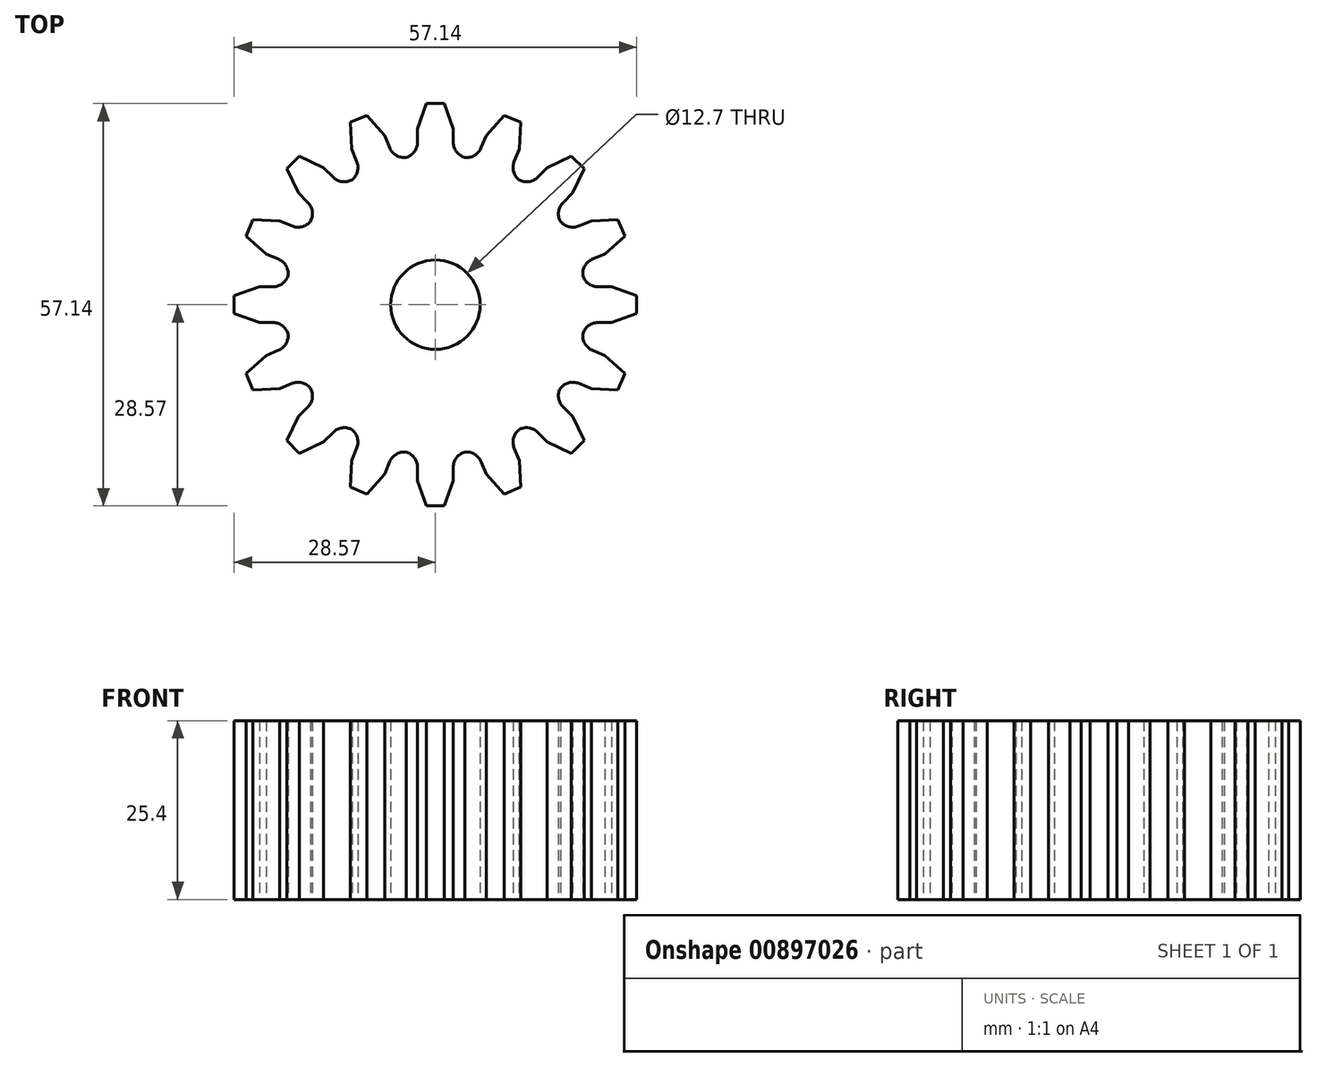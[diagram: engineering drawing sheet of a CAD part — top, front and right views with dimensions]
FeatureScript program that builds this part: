
annotation { "Feature Type Name" : "Feature", "Feature Type Description" : "" }
export const myFeature = defineFeature(function(context is Context, id is Id, definition is map)
    precondition{}
    {
        {
            var Q0;
            Q0=qCreatedBy(makeId("Top.planeOp"),FACE);
            var sketch = newSketch(context, id + "F0", { "sketchPlane" : qUnion([Q0])});
            skCircle(sketch, "E0", {"center": v(0, 0) * mm, "radius": 6.35 * mm});
            skLineSegment(sketch, "E1", {"start": v(0, 28.58) * mm, "end": v(1.27, 28.58) * mm});
            skLineSegment(sketch, "E2", {"start": v(0, 28.58) * mm, "end": v(-1.27, 28.58) * mm});
            skLineSegment(sketch, "E3", {"start": v(-1.27, 28.58) * mm, "end": v(-2.54, 24.98) * mm});
            skLineSegment(sketch, "E4", {"start": v(2.54, 24.98) * mm, "end": v(1.27, 28.58) * mm});
            skPoint(sketch, "E5.MirrorCS.start.orphan", {"position": v(-2.54, 28.58) * mm});
            skPoint(sketch, "E6.orphan", {"position": v(2.54, 28.58) * mm});
            skLineSegment(sketch, "E7.1.2", {"start": v(-12.1, 25.91) * mm, "end": v(-11.9, 22.1) * mm});
            skLineSegment(sketch, "E7.1.4", {"start": v(-7.21, 24.05) * mm, "end": v(-9.76, 26.89) * mm});
            skLineSegment(sketch, "E7.1.5", {"start": v(-10.94, 26.4) * mm, "end": v(-12.1, 25.91) * mm});
            skLineSegment(sketch, "E7.1.6", {"start": v(-10.94, 26.4) * mm, "end": v(-9.76, 26.89) * mm});
            skLineSegment(sketch, "E7.2.2", {"start": v(-21.1, 19.3) * mm, "end": v(-19.46, 15.87) * mm});
            skLineSegment(sketch, "E7.2.4", {"start": v(-15.87, 19.46) * mm, "end": v(-19.3, 21.1) * mm});
            skLineSegment(sketch, "E7.2.5", {"start": v(-20.2, 20.2) * mm, "end": v(-21.1, 19.3) * mm});
            skLineSegment(sketch, "E7.2.6", {"start": v(-20.2, 20.2) * mm, "end": v(-19.3, 21.1) * mm});
            skLineSegment(sketch, "E7.3.2", {"start": v(-26.89, 9.76) * mm, "end": v(-24.05, 7.21) * mm});
            skLineSegment(sketch, "E7.3.4", {"start": v(-22.1, 11.9) * mm, "end": v(-25.91, 12.1) * mm});
            skLineSegment(sketch, "E7.3.5", {"start": v(-26.4, 10.94) * mm, "end": v(-26.89, 9.76) * mm});
            skLineSegment(sketch, "E7.3.6", {"start": v(-26.4, 10.94) * mm, "end": v(-25.91, 12.1) * mm});
            skLineSegment(sketch, "E7.4.2", {"start": v(-28.58, -1.27) * mm, "end": v(-24.98, -2.54) * mm});
            skLineSegment(sketch, "E7.4.4", {"start": v(-24.98, 2.54) * mm, "end": v(-28.58, 1.27) * mm});
            skLineSegment(sketch, "E7.4.5", {"start": v(-28.58, 0) * mm, "end": v(-28.58, -1.27) * mm});
            skLineSegment(sketch, "E7.4.6", {"start": v(-28.58, 0) * mm, "end": v(-28.58, 1.27) * mm});
            skLineSegment(sketch, "E7.5.1", {"start": v(-22.1, -11.9) * mm, "end": v(-20.34, -11.18) * mm});
            skLineSegment(sketch, "E7.5.2", {"start": v(-25.91, -12.1) * mm, "end": v(-22.1, -11.9) * mm});
            skLineSegment(sketch, "E7.5.4", {"start": v(-24.05, -7.21) * mm, "end": v(-26.89, -9.76) * mm});
            skLineSegment(sketch, "E7.5.5", {"start": v(-26.4, -10.94) * mm, "end": v(-25.91, -12.1) * mm});
            skLineSegment(sketch, "E7.5.6", {"start": v(-26.4, -10.94) * mm, "end": v(-26.89, -9.76) * mm});
            skLineSegment(sketch, "E7.6.2", {"start": v(-19.3, -21.1) * mm, "end": v(-15.87, -19.46) * mm});
            skLineSegment(sketch, "E7.6.3", {"start": v(-19.46, -15.87) * mm, "end": v(-18.11, -14.52) * mm});
            skLineSegment(sketch, "E7.6.4", {"start": v(-19.46, -15.87) * mm, "end": v(-21.1, -19.3) * mm});
            skLineSegment(sketch, "E7.6.5", {"start": v(-20.2, -20.2) * mm, "end": v(-19.3, -21.1) * mm});
            skLineSegment(sketch, "E7.6.6", {"start": v(-20.2, -20.2) * mm, "end": v(-21.1, -19.3) * mm});
            skLineSegment(sketch, "E7.7.2", {"start": v(-9.76, -26.89) * mm, "end": v(-7.21, -24.05) * mm});
            skLineSegment(sketch, "E7.7.4", {"start": v(-11.9, -22.1) * mm, "end": v(-12.1, -25.91) * mm});
            skLineSegment(sketch, "E7.7.5", {"start": v(-10.94, -26.4) * mm, "end": v(-9.76, -26.89) * mm});
            skLineSegment(sketch, "E7.7.6", {"start": v(-10.94, -26.4) * mm, "end": v(-12.1, -25.91) * mm});
            skLineSegment(sketch, "E7.8.2", {"start": v(1.27, -28.58) * mm, "end": v(2.54, -24.98) * mm});
            skLineSegment(sketch, "E7.8.4", {"start": v(-2.54, -24.98) * mm, "end": v(-1.27, -28.58) * mm});
            skLineSegment(sketch, "E7.8.5", {"start": v(0, -28.58) * mm, "end": v(1.27, -28.58) * mm});
            skLineSegment(sketch, "E7.8.6", {"start": v(0, -28.58) * mm, "end": v(-1.27, -28.58) * mm});
            skLineSegment(sketch, "E7.9.2", {"start": v(12.1, -25.91) * mm, "end": v(11.9, -22.1) * mm});
            skLineSegment(sketch, "E7.9.4", {"start": v(7.21, -24.05) * mm, "end": v(9.76, -26.89) * mm});
            skLineSegment(sketch, "E7.9.5", {"start": v(10.94, -26.4) * mm, "end": v(12.1, -25.91) * mm});
            skLineSegment(sketch, "E7.9.6", {"start": v(10.94, -26.4) * mm, "end": v(9.76, -26.89) * mm});
            skLineSegment(sketch, "E7.10.2", {"start": v(21.1, -19.3) * mm, "end": v(19.46, -15.87) * mm});
            skLineSegment(sketch, "E7.10.3", {"start": v(15.87, -19.46) * mm, "end": v(13.18, -16.78) * mm});
            skLineSegment(sketch, "E7.10.4", {"start": v(15.87, -19.46) * mm, "end": v(19.3, -21.1) * mm});
            skLineSegment(sketch, "E7.10.5", {"start": v(20.2, -20.2) * mm, "end": v(21.1, -19.3) * mm});
            skLineSegment(sketch, "E7.10.6", {"start": v(20.2, -20.2) * mm, "end": v(19.3, -21.1) * mm});
            skLineSegment(sketch, "E7.11.2", {"start": v(26.89, -9.76) * mm, "end": v(24.05, -7.21) * mm});
            skLineSegment(sketch, "E7.11.4", {"start": v(22.1, -11.9) * mm, "end": v(25.91, -12.1) * mm});
            skLineSegment(sketch, "E7.11.5", {"start": v(26.4, -10.94) * mm, "end": v(26.89, -9.76) * mm});
            skLineSegment(sketch, "E7.11.6", {"start": v(26.4, -10.94) * mm, "end": v(25.91, -12.1) * mm});
            skLineSegment(sketch, "E7.12.2", {"start": v(28.58, 1.27) * mm, "end": v(24.98, 2.54) * mm});
            skLineSegment(sketch, "E7.12.4", {"start": v(24.98, -2.54) * mm, "end": v(28.58, -1.27) * mm});
            skLineSegment(sketch, "E7.12.5", {"start": v(28.58, 0) * mm, "end": v(28.58, 1.27) * mm});
            skLineSegment(sketch, "E7.12.6", {"start": v(28.58, 0) * mm, "end": v(28.58, -1.27) * mm});
            skLineSegment(sketch, "E7.13.2", {"start": v(25.91, 12.1) * mm, "end": v(22.1, 11.9) * mm});
            skLineSegment(sketch, "E7.13.4", {"start": v(24.05, 7.21) * mm, "end": v(26.89, 9.76) * mm});
            skLineSegment(sketch, "E7.13.5", {"start": v(26.4, 10.94) * mm, "end": v(25.91, 12.1) * mm});
            skLineSegment(sketch, "E7.13.6", {"start": v(26.4, 10.94) * mm, "end": v(26.89, 9.76) * mm});
            skLineSegment(sketch, "E7.14.2", {"start": v(19.3, 21.1) * mm, "end": v(15.87, 19.46) * mm});
            skLineSegment(sketch, "E7.14.4", {"start": v(19.46, 15.87) * mm, "end": v(21.1, 19.3) * mm});
            skLineSegment(sketch, "E7.14.5", {"start": v(20.2, 20.2) * mm, "end": v(19.3, 21.1) * mm});
            skLineSegment(sketch, "E7.14.6", {"start": v(20.2, 20.2) * mm, "end": v(21.1, 19.3) * mm});
            skLineSegment(sketch, "E7.15.2", {"start": v(9.76, 26.89) * mm, "end": v(7.21, 24.05) * mm});
            skLineSegment(sketch, "E7.15.4", {"start": v(11.9, 22.1) * mm, "end": v(12.1, 25.91) * mm});
            skLineSegment(sketch, "E7.15.5", {"start": v(10.94, 26.4) * mm, "end": v(9.76, 26.89) * mm});
            skLineSegment(sketch, "E7.15.6", {"start": v(10.94, 26.4) * mm, "end": v(12.1, 25.91) * mm});
            skPoint(sketch, "E8.visualSharp", {"position": v(-21.18, -2.54) * mm});
            skArc(sketch, "E8.filletArc", {"start": v(-20.93, -4.16) * mm, "mid": v(-21.73, -3) * mm, "end": v(-23.07, -2.54) * mm});
            skPoint(sketch, "E9.visualSharp", {"position": v(-20.54, -5.76) * mm});
            skArc(sketch, "E9.filletArc", {"start": v(-22.29, -6.48) * mm, "mid": v(-21.22, -5.55) * mm, "end": v(-20.93, -4.16) * mm});
            skArc(sketch, "E10.1.1", {"start": v(-17.75, -11.86) * mm, "mid": v(-18.93, -11.08) * mm, "end": v(-20.34, -11.18) * mm});
            skArc(sketch, "E10.1.2", {"start": v(-18.11, -14.52) * mm, "mid": v(-17.48, -13.25) * mm, "end": v(-17.75, -11.86) * mm});
            skArc(sketch, "E10.2.1", {"start": v(-11.73, -17.83) * mm, "mid": v(-13.17, -17.47) * mm, "end": v(-14.52, -18.11) * mm});
            skArc(sketch, "E10.2.2", {"start": v(-11.18, -20.34) * mm, "mid": v(-11.1, -18.86) * mm, "end": v(-11.98, -17.65) * mm});
            skArc(sketch, "E10.3.1", {"start": v(-4.01, -20.96) * mm, "mid": v(-5.48, -21.18) * mm, "end": v(-6.48, -22.29) * mm});
            skArc(sketch, "E10.3.2", {"start": v(-2.54, -23.07) * mm, "mid": v(-3.04, -21.67) * mm, "end": v(-4.31, -20.9) * mm});
            skArc(sketch, "E10.4.1", {"start": v(4.31, -20.9) * mm, "mid": v(3.04, -21.67) * mm, "end": v(2.54, -23.07) * mm});
            skArc(sketch, "E10.4.2", {"start": v(6.48, -22.29) * mm, "mid": v(5.48, -21.18) * mm, "end": v(4.01, -20.96) * mm});
            skArc(sketch, "E10.5.1", {"start": v(11.98, -17.65) * mm, "mid": v(11.1, -18.86) * mm, "end": v(11.18, -20.34) * mm});
            skArc(sketch, "E10.5.2", {"start": v(14.52, -18.11) * mm, "mid": v(13.17, -17.47) * mm, "end": v(11.73, -17.83) * mm});
            skArc(sketch, "E10.6.1", {"start": v(17.83, -11.73) * mm, "mid": v(17.47, -13.17) * mm, "end": v(18.11, -14.52) * mm});
            skArc(sketch, "E10.6.2", {"start": v(20.34, -11.18) * mm, "mid": v(18.86, -11.1) * mm, "end": v(17.65, -11.98) * mm});
            skArc(sketch, "E10.7.1", {"start": v(20.93, -4.16) * mm, "mid": v(21.22, -5.55) * mm, "end": v(22.29, -6.48) * mm});
            skArc(sketch, "E10.7.2", {"start": v(23.07, -2.54) * mm, "mid": v(21.73, -3) * mm, "end": v(20.93, -4.16) * mm});
            skArc(sketch, "E10.8.1", {"start": v(20.93, 4.16) * mm, "mid": v(21.73, 3) * mm, "end": v(23.07, 2.54) * mm});
            skArc(sketch, "E10.8.2", {"start": v(22.29, 6.48) * mm, "mid": v(21.22, 5.55) * mm, "end": v(20.93, 4.16) * mm});
            skArc(sketch, "E10.9.1", {"start": v(17.75, 11.86) * mm, "mid": v(18.93, 11.08) * mm, "end": v(20.34, 11.18) * mm});
            skArc(sketch, "E10.9.2", {"start": v(18.11, 14.52) * mm, "mid": v(17.48, 13.25) * mm, "end": v(17.75, 11.86) * mm});
            skArc(sketch, "E10.10.1", {"start": v(11.86, 17.75) * mm, "mid": v(13.25, 17.48) * mm, "end": v(14.52, 18.11) * mm});
            skArc(sketch, "E10.10.2", {"start": v(11.18, 20.34) * mm, "mid": v(11.08, 18.93) * mm, "end": v(11.86, 17.75) * mm});
            skArc(sketch, "E10.11.1", {"start": v(4.16, 20.93) * mm, "mid": v(5.55, 21.22) * mm, "end": v(6.48, 22.29) * mm});
            skArc(sketch, "E10.11.2", {"start": v(2.54, 23.07) * mm, "mid": v(3, 21.73) * mm, "end": v(4.16, 20.93) * mm});
            skArc(sketch, "E10.12.1", {"start": v(-4.16, 20.93) * mm, "mid": v(-3, 21.73) * mm, "end": v(-2.54, 23.07) * mm});
            skArc(sketch, "E10.12.2", {"start": v(-6.48, 22.29) * mm, "mid": v(-5.55, 21.22) * mm, "end": v(-4.16, 20.93) * mm});
            skArc(sketch, "E10.13.1", {"start": v(-11.86, 17.75) * mm, "mid": v(-11.08, 18.93) * mm, "end": v(-11.18, 20.34) * mm});
            skArc(sketch, "E10.13.2", {"start": v(-14.52, 18.11) * mm, "mid": v(-13.25, 17.48) * mm, "end": v(-11.86, 17.75) * mm});
            skArc(sketch, "E10.14.1", {"start": v(-17.75, 11.86) * mm, "mid": v(-17.48, 13.25) * mm, "end": v(-18.11, 14.52) * mm});
            skArc(sketch, "E10.14.2", {"start": v(-20.34, 11.18) * mm, "mid": v(-18.93, 11.08) * mm, "end": v(-17.75, 11.86) * mm});
            skArc(sketch, "E10.15.1", {"start": v(-20.93, 4.16) * mm, "mid": v(-21.22, 5.55) * mm, "end": v(-22.29, 6.48) * mm});
            skArc(sketch, "E10.15.2", {"start": v(-23.07, 2.54) * mm, "mid": v(-21.73, 3) * mm, "end": v(-20.93, 4.16) * mm});
            skPoint(sketch, "E11.orphan", {"position": v(-21.18, 2.54) * mm});
            skPoint(sketch, "E12.orphan", {"position": v(-16.78, 13.18) * mm});
            skPoint(sketch, "E13.orphan", {"position": v(-18.6, 10.45) * mm});
            skPoint(sketch, "E14.orphan", {"position": v(-20.54, 5.76) * mm});
            skPoint(sketch, "E15.orphan", {"position": v(-20.9, -4.31) * mm});
            skPoint(sketch, "E16.orphan", {"position": v(-18.6, -10.45) * mm});
            skPoint(sketch, "E17.orphan", {"position": v(-16.78, -13.18) * mm});
            skPoint(sketch, "E18.orphan", {"position": v(-17.83, -11.73) * mm});
            skPoint(sketch, "E19.orphan", {"position": v(-17.65, -11.98) * mm});
            skPoint(sketch, "E20.orphan", {"position": v(-13.18, 16.78) * mm});
            skPoint(sketch, "E21.orphan", {"position": v(-10.45, 18.6) * mm});
            skPoint(sketch, "E22.orphan", {"position": v(-11.98, 17.65) * mm});
            skPoint(sketch, "E23.orphan", {"position": v(-11.73, 17.83) * mm});
            skPoint(sketch, "E24.orphan", {"position": v(-4.31, 20.9) * mm});
            skPoint(sketch, "E25.orphan", {"position": v(-4.01, 20.96) * mm});
            skPoint(sketch, "E26.orphan", {"position": v(-5.76, 20.54) * mm});
            skPoint(sketch, "E27.orphan", {"position": v(-2.54, 21.18) * mm});
            skPoint(sketch, "E28.orphan", {"position": v(2.54, 21.18) * mm});
            skPoint(sketch, "E29.orphan", {"position": v(4.01, 20.96) * mm});
            skPoint(sketch, "E30.orphan", {"position": v(4.31, 20.9) * mm});
            skPoint(sketch, "E31.orphan", {"position": v(5.76, 20.54) * mm});
            skPoint(sketch, "E32.orphan", {"position": v(10.45, 18.6) * mm});
            skPoint(sketch, "E33.orphan", {"position": v(13.18, 16.78) * mm});
            skPoint(sketch, "E34.orphan", {"position": v(11.73, 17.83) * mm});
            skPoint(sketch, "E35.orphan", {"position": v(11.98, 17.65) * mm});
            skPoint(sketch, "E36.orphan", {"position": v(16.78, 13.18) * mm});
            skPoint(sketch, "E37.orphan", {"position": v(18.6, 10.45) * mm});
            skPoint(sketch, "E38.orphan", {"position": v(17.83, 11.73) * mm});
            skPoint(sketch, "E39.orphan", {"position": v(17.65, 11.98) * mm});
            skPoint(sketch, "E40.orphan", {"position": v(20.54, 5.76) * mm});
            skPoint(sketch, "E41.orphan", {"position": v(21.18, 2.54) * mm});
            skPoint(sketch, "E42.orphan", {"position": v(20.9, 4.31) * mm});
            skPoint(sketch, "E43.orphan", {"position": v(20.96, 4.01) * mm});
            skPoint(sketch, "E44.orphan", {"position": v(20.54, -5.76) * mm});
            skPoint(sketch, "E45.orphan", {"position": v(20.96, -4.01) * mm});
            skPoint(sketch, "E46.orphan", {"position": v(20.9, -4.31) * mm});
            skLineSegment(sketch, "E47.1.1", {"start": v(-15.87, -19.46) * mm, "end": v(-14.52, -18.11) * mm});
            skLineSegment(sketch, "E47.1.2", {"start": v(-11.9, -22.1) * mm, "end": v(-11.18, -20.34) * mm});
            skLineSegment(sketch, "E47.2.1", {"start": v(-7.21, -24.05) * mm, "end": v(-6.48, -22.29) * mm});
            skLineSegment(sketch, "E47.2.2", {"start": v(-2.54, -24.98) * mm, "end": v(-2.54, -23.07) * mm});
            skLineSegment(sketch, "E47.3.1", {"start": v(2.54, -24.98) * mm, "end": v(2.54, -23.07) * mm});
            skLineSegment(sketch, "E47.3.2", {"start": v(7.21, -24.05) * mm, "end": v(6.48, -22.29) * mm});
            skLineSegment(sketch, "E47.4.1", {"start": v(11.9, -22.1) * mm, "end": v(11.18, -20.34) * mm});
            skLineSegment(sketch, "E47.4.2", {"start": v(15.87, -19.46) * mm, "end": v(14.52, -18.11) * mm});
            skLineSegment(sketch, "E47.5.1", {"start": v(19.46, -15.87) * mm, "end": v(18.11, -14.52) * mm});
            skLineSegment(sketch, "E47.5.2", {"start": v(22.1, -11.9) * mm, "end": v(20.34, -11.18) * mm});
            skLineSegment(sketch, "E47.6.1", {"start": v(24.05, -7.21) * mm, "end": v(22.29, -6.48) * mm});
            skLineSegment(sketch, "E47.6.2", {"start": v(24.98, -2.54) * mm, "end": v(23.07, -2.54) * mm});
            skLineSegment(sketch, "E47.7.1", {"start": v(24.98, 2.54) * mm, "end": v(23.07, 2.54) * mm});
            skLineSegment(sketch, "E47.7.2", {"start": v(24.05, 7.21) * mm, "end": v(22.29, 6.48) * mm});
            skLineSegment(sketch, "E47.8.1", {"start": v(22.1, 11.9) * mm, "end": v(20.34, 11.18) * mm});
            skLineSegment(sketch, "E47.8.2", {"start": v(19.46, 15.87) * mm, "end": v(18.11, 14.52) * mm});
            skLineSegment(sketch, "E47.9.1", {"start": v(15.87, 19.46) * mm, "end": v(14.52, 18.11) * mm});
            skLineSegment(sketch, "E47.9.2", {"start": v(11.9, 22.1) * mm, "end": v(11.18, 20.34) * mm});
            skLineSegment(sketch, "E47.10.1", {"start": v(7.21, 24.05) * mm, "end": v(6.48, 22.29) * mm});
            skLineSegment(sketch, "E47.10.2", {"start": v(2.54, 24.98) * mm, "end": v(2.54, 23.07) * mm});
            skLineSegment(sketch, "E47.11.1", {"start": v(-2.54, 24.98) * mm, "end": v(-2.54, 23.07) * mm});
            skLineSegment(sketch, "E47.11.2", {"start": v(-7.21, 24.05) * mm, "end": v(-6.48, 22.29) * mm});
            skLineSegment(sketch, "E47.12.1", {"start": v(-11.9, 22.1) * mm, "end": v(-11.18, 20.34) * mm});
            skLineSegment(sketch, "E47.12.2", {"start": v(-15.87, 19.46) * mm, "end": v(-14.52, 18.11) * mm});
            skLineSegment(sketch, "E47.13.1", {"start": v(-19.46, 15.87) * mm, "end": v(-18.11, 14.52) * mm});
            skLineSegment(sketch, "E47.13.2", {"start": v(-22.1, 11.9) * mm, "end": v(-20.34, 11.18) * mm});
            skLineSegment(sketch, "E47.14.1", {"start": v(-24.05, 7.21) * mm, "end": v(-22.29, 6.48) * mm});
            skLineSegment(sketch, "E47.14.2", {"start": v(-24.98, 2.54) * mm, "end": v(-23.07, 2.54) * mm});
            skLineSegment(sketch, "E47.15.1", {"start": v(-24.98, -2.54) * mm, "end": v(-23.07, -2.54) * mm});
            skLineSegment(sketch, "E47.15.2", {"start": v(-24.05, -7.21) * mm, "end": v(-22.29, -6.48) * mm});
            skSolve(sketch);
        }
        {
            var Q0;
            Q0=makeQuery(id+"F0.imprint","IMPRINT",FACE,{"disambiguationData":[TD([[makeQuery(id+"F0.imprint","IMPRINT",EDGE,{"derivedFrom":sQuery(id+"F0.wireOp",EDGE,"E1")}),-1.0]])]});
            extrude(context, id + "F1", {"entities" : qUnion([Q0]), "depth" : 25.4 * mm, "offsetDistance" : 25.4 * mm});
        }
    });
